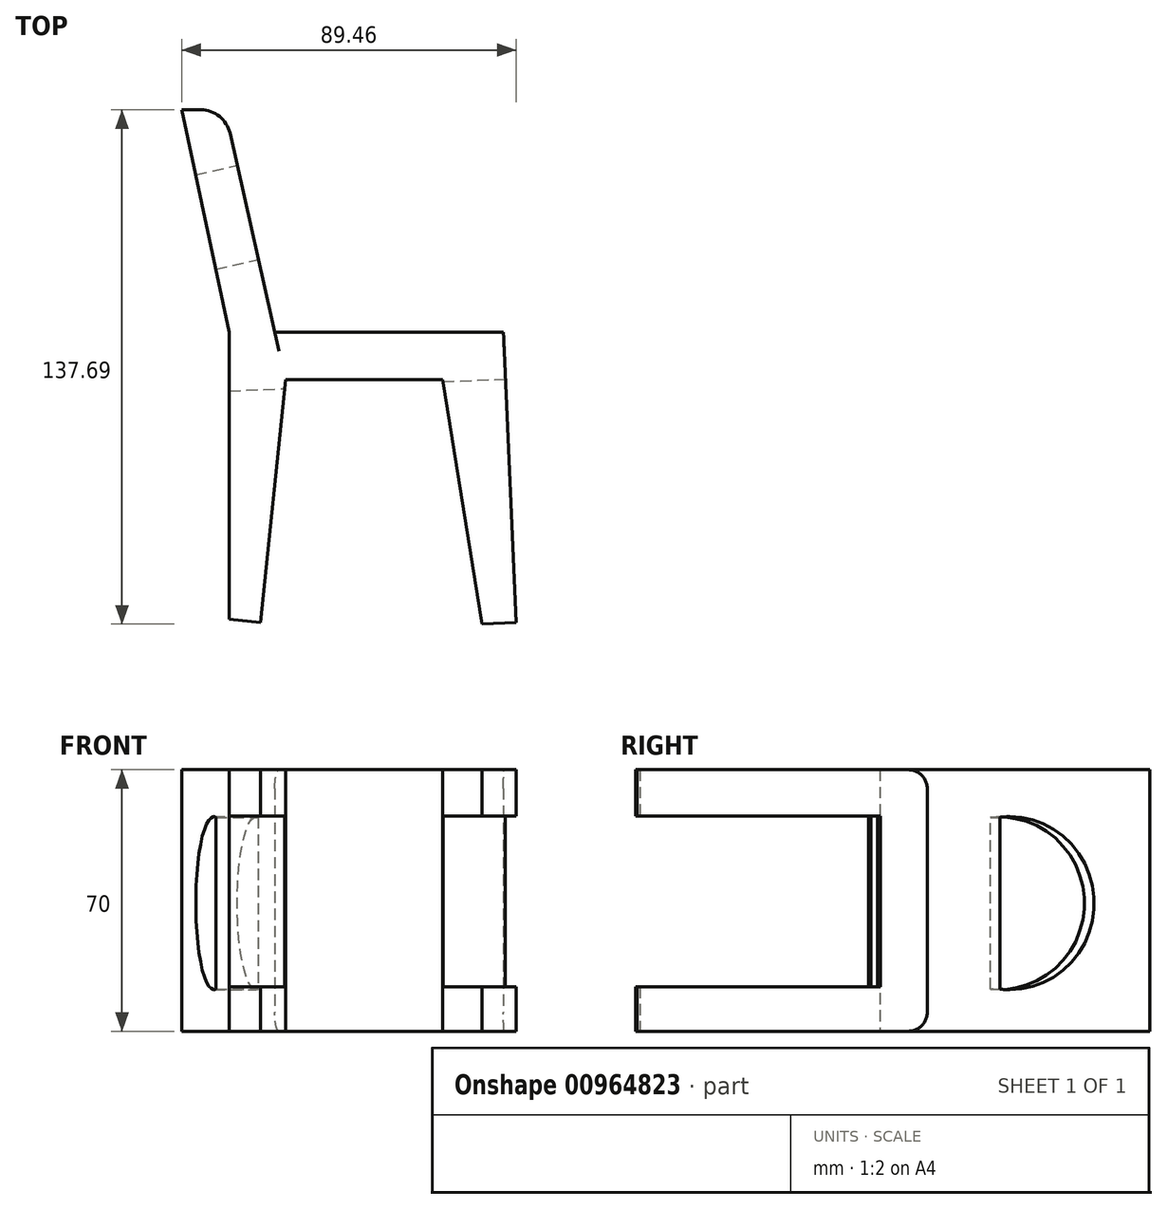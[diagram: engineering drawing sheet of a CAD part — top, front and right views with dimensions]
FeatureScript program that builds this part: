
annotation { "Feature Type Name" : "Feature", "Feature Type Description" : "" }
export const myFeature = defineFeature(function(context is Context, id is Id, definition is map)
    precondition{}
    {
        {
            var Q0;
            Q0=qCreatedBy(makeId("Top.planeOp"),FACE);
            var sketch = newSketch(context, id + "F0", { "sketchPlane" : qUnion([Q0])});
            skLineSegment(sketch, "E0", {"start": v(-58.6, 59.56) * mm, "end": v(-47.12, 59.56) * mm});
            skLineSegment(sketch, "E1", {"start": v(-47.12, 59.56) * mm, "end": v(-33.73, 0) * mm});
            skLineSegment(sketch, "E2", {"start": v(-33.73, 0) * mm, "end": v(27.5, 0) * mm});
            skLineSegment(sketch, "E3", {"start": v(27.5, 0) * mm, "end": v(30.86, -77.74) * mm});
            skLineSegment(sketch, "E4", {"start": v(30.86, -77.74) * mm, "end": v(21.78, -78.13) * mm});
            skLineSegment(sketch, "E5", {"start": v(21.78, -78.13) * mm, "end": v(11.24, -12.68) * mm});
            skLineSegment(sketch, "E6", {"start": v(11.24, -12.68) * mm, "end": v(-30.86, -12.68) * mm});
            skLineSegment(sketch, "E7", {"start": v(-30.86, -12.68) * mm, "end": v(-37.55, -77.74) * mm});
            skLineSegment(sketch, "E8", {"start": v(-37.55, -77.74) * mm, "end": v(-45.93, -76.87) * mm});
            skLineSegment(sketch, "E9", {"start": v(-45.93, -76.87) * mm, "end": v(-45.93, 0) * mm});
            skLineSegment(sketch, "E10", {"start": v(-45.93, 0) * mm, "end": v(-58.6, 59.56) * mm});
            skSolve(sketch);
        }
        {
            var Q0;
            Q0 = qSketchRegion(id + "F0", true);
            extrude(context, id + "F1", {"entities" : qUnion([Q0]), "depth" : 70 * mm, "offsetDistance" : 25 * mm});
        }
        {
            var Q0;
            Q0=makeQuery(id+"F1.opExtrude","SWEPT_FACE",FACE,{"disambiguationData":[OSD([sQuery(id+"F0.wireOp",EDGE,"E3")])]});
            var sketch = newSketch(context, id + "F2", { "sketchPlane" : qUnion([Q0])});
            skLineSegment(sketch, "E11.bottom", {"start": v(-13.72, 57.6) * mm, "end": v(-79, 57.6) * mm});
            skLineSegment(sketch, "E11.top", {"start": v(-13.72, 11.89) * mm, "end": v(-79, 11.89) * mm});
            skLineSegment(sketch, "E11.left", {"start": v(-13.72, 57.6) * mm, "end": v(-13.72, 11.89) * mm});
            skLineSegment(sketch, "E11.right", {"start": v(-79, 57.6) * mm, "end": v(-79, 11.89) * mm});
            skSolve(sketch);
        }
        {
            var Q0;
            Q0 = qSketchRegion(id + "F2", true);
            extrude(context, id + "F3", {"entities" : qUnion([Q0]), "operationType" : NewBodyOperationType.REMOVE, "oppositeDirection" : true, "depth" : 127.5 * mm, "offsetDistance" : 25 * mm});
        }
        {
            var Q0;
            Q0=makeQuery(id+"F1.opExtrude","SWEPT_FACE",FACE,{"disambiguationData":[OSD([sQuery(id+"F0.wireOp",EDGE,"E1")])]});
            var sketch = newSketch(context, id + "F4", { "sketchPlane" : qUnion([Q0])});
            skArc(sketch, "E12", {"start": v(27.39, 11.27) * mm, "mid": v(53.2, 34.28) * mm, "end": v(27.39, 57.29) * mm});
            skLineSegment(sketch, "E13", {"start": v(27.39, 57.29) * mm, "end": v(27.39, 11.27) * mm});
            skSolve(sketch);
        }
        {
            var Q0;
            Q0=makeQuery(id+"F4.imprint","IMPRINT",FACE,{"disambiguationData":[TD([[makeQuery(id+"F4.imprint","IMPRINT",EDGE,{"derivedFrom":sQuery(id+"F4.wireOp",EDGE,"E12")}),1.0]])]});
            extrude(context, id + "F5", {"entities" : qUnion([Q0]), "operationType" : NewBodyOperationType.REMOVE, "oppositeDirection" : true, "depth" : 41.3 * mm, "offsetDistance" : 25 * mm});
        }
        {
            var Q0;
            Q0=makeQuery(id+"F1.opExtrude","CAP_EDGE",EDGE,{"disambiguationData":[OSD([sQuery(id+"F0.wireOp",EDGE,"E2")])],"isStart":true});
            var Q1;
            Q1=makeQuery(id+"F1.opExtrude","CAP_EDGE",EDGE,{"disambiguationData":[OSD([sQuery(id+"F0.wireOp",EDGE,"E2")])],"isStart":false});
            fillet(context, id + "F6", {"entities" : qUnion([Q0, Q1]), "radius" : 5 * mm, "tangentPropagation" : true, "allowEdgeOverflow" : false});
        }
        {
            var Q0;
            Q0=makeQuery(id+"F1.opExtrude","SWEPT_EDGE",EDGE,{"disambiguationData":[OSD([sQuery(id+"F0.wireOp",EDGE,"E0"),sQuery(id+"F0.wireOp",EDGE,"E1")])]});
            fillet(context, id + "F7", {"entities" : qUnion([Q0]), "radius" : 8 * mm, "tangentPropagation" : true, "allowEdgeOverflow" : false});
        }
    });
